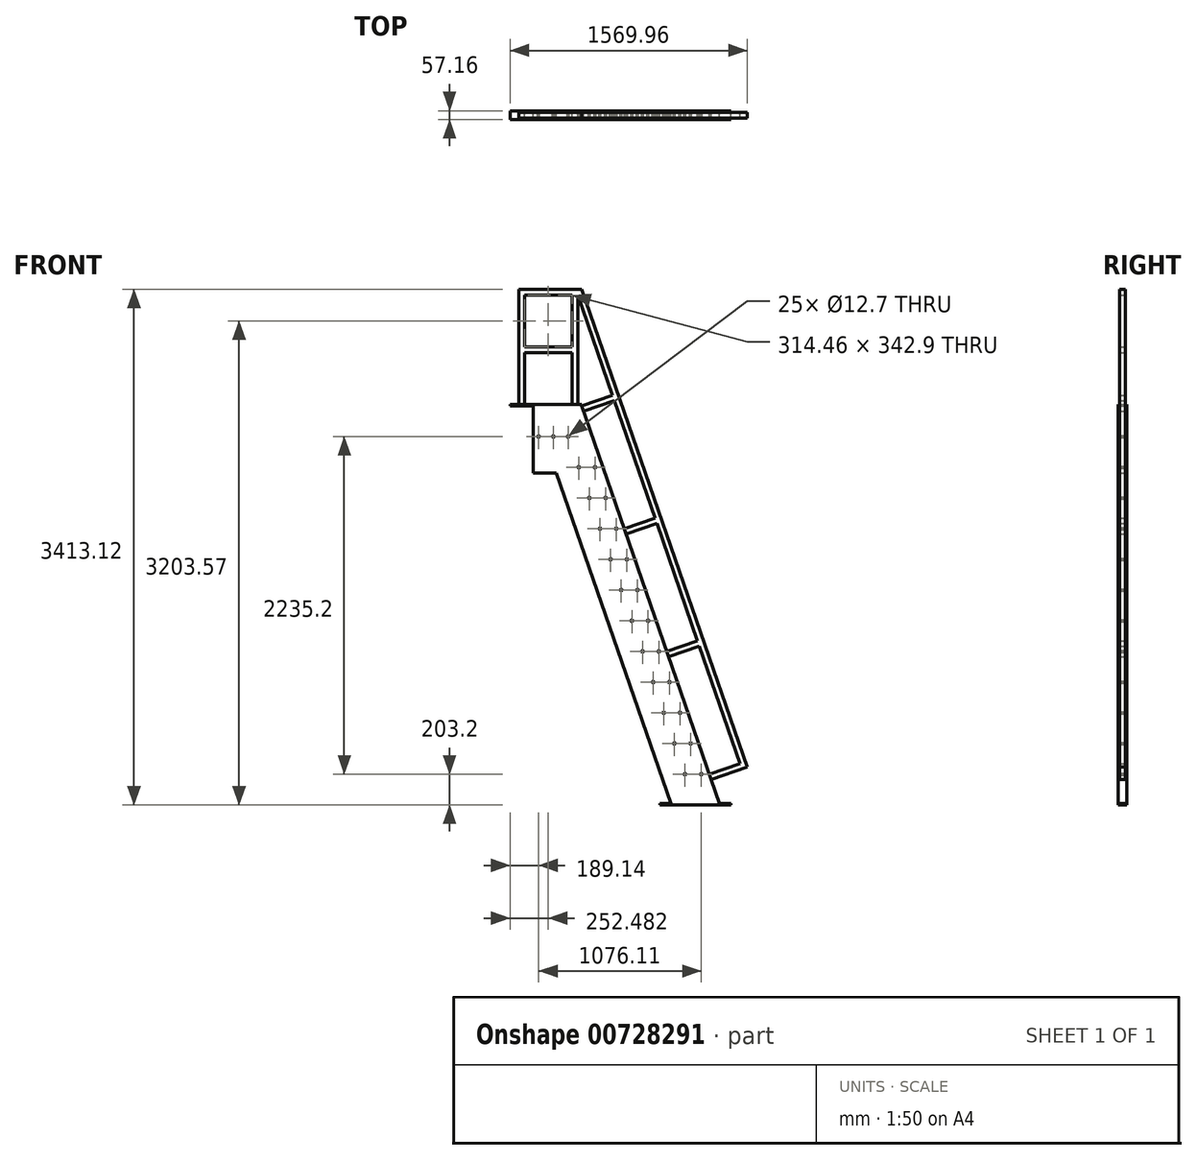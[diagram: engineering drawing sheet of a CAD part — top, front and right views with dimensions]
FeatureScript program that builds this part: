
annotation { "Feature Type Name" : "Feature", "Feature Type Description" : "" }
export const myFeature = defineFeature(function(context is Context, id is Id, definition is map)
    precondition{}
    {
        {
            var Q0;
            Q0=qCreatedBy(makeId("Front.planeOp"),FACE);
            var sketch = newSketch(context, id + "F0", { "sketchPlane" : qUnion([Q0])});
            skLineSegment(sketch, "E0", {"start": v(0, 2641.6) * mm, "end": v(0, 0) * mm, "construction": true});
            skLineSegment(sketch, "E1", {"start": v(0, 0) * mm, "end": v(914.4, 0) * mm, "construction": true});
            skLineSegment(sketch, "E2", {"start": v(0, 2641.6) * mm, "end": v(914.4, 0) * mm});
            skLineSegment(sketch, "E3", {"start": v(0, 2641.6) * mm, "end": v(322.54, 2641.6) * mm});
            skLineSegment(sketch, "E4", {"start": v(914.4, 0) * mm, "end": v(1236.94, 0) * mm});
            skLineSegment(sketch, "E5", {"start": v(322.54, 2641.6) * mm, "end": v(565.8, 1938.87) * mm});
            skLineSegment(sketch, "E6", {"start": v(0, 2641.6) * mm, "end": v(0, 2438.4) * mm, "construction": true});
            skLineSegment(sketch, "E7", {"start": v(0, 2438.4) * mm, "end": v(392.88, 2438.4) * mm, "construction": true});
            skLineSegment(sketch, "E8", {"start": v(0, 2438.4) * mm, "end": v(0, 2235.2) * mm, "construction": true});
            skLineSegment(sketch, "E9", {"start": v(0, 2235.2) * mm, "end": v(914.4, 2235.2) * mm, "construction": true});
            skLineSegment(sketch, "E10.0", {"start": v(0, 2032) * mm, "end": v(914.4, 2032) * mm, "construction": true});
            skLineSegment(sketch, "E11.0", {"start": v(0, 1828.8) * mm, "end": v(914.4, 1828.8) * mm, "construction": true});
            skLineSegment(sketch, "E12.0", {"start": v(0, 1625.6) * mm, "end": v(914.4, 1625.6) * mm, "construction": true});
            skLineSegment(sketch, "E13.0", {"start": v(0, 1422.4) * mm, "end": v(914.4, 1422.4) * mm, "construction": true});
            skLineSegment(sketch, "E14.0", {"start": v(0, 1219.2) * mm, "end": v(914.4, 1219.2) * mm, "construction": true});
            skLineSegment(sketch, "E15.0", {"start": v(0, 1016) * mm, "end": v(914.4, 1016) * mm, "construction": true});
            skLineSegment(sketch, "E16.0", {"start": v(0, 812.8) * mm, "end": v(955.6, 812.8) * mm, "construction": true});
            skLineSegment(sketch, "E17.0", {"start": v(0, 609.6) * mm, "end": v(1025.93, 609.6) * mm, "construction": true});
            skLineSegment(sketch, "E18", {"start": v(0, 609.6) * mm, "end": v(0, 406.4) * mm, "construction": true});
            skLineSegment(sketch, "E19", {"start": v(0, 406.4) * mm, "end": v(1272.26, 406.4) * mm, "construction": true});
            skLineSegment(sketch, "E20.0", {"start": v(0, 203.2) * mm, "end": v(1272.26, 203.2) * mm, "construction": true});
            skLineSegment(sketch, "E21", {"start": v(161.27, 2641.6) * mm, "end": v(1075.67, 0) * mm, "construction": true});
            skLineSegment(sketch, "E22.0", {"start": v(257.28, 2674.83) * mm, "end": v(1171.68, 33.23) * mm, "construction": true});
            skCircle(sketch, "E23", {"center": v(935, 406.4) * mm, "radius": 6.35 * mm});
            skCircle(sketch, "E24", {"center": v(1042.51, 406.4) * mm, "radius": 6.35 * mm});
            skCircle(sketch, "E25", {"center": v(1005.33, 203.2) * mm, "radius": 6.35 * mm});
            skCircle(sketch, "E26", {"center": v(1112.85, 203.2) * mm, "radius": 6.35 * mm});
            skLineSegment(sketch, "E27", {"start": v(322.54, 2641.6) * mm, "end": v(322.54, 2651.13) * mm});
            skLineSegment(sketch, "E28", {"start": v(322.54, 2651.13) * mm, "end": v(0, 2651.13) * mm});
            skLineSegment(sketch, "E29", {"start": v(0, 2651.13) * mm, "end": v(0, 2641.6) * mm});
            skLineSegment(sketch, "E30", {"start": v(0, 2651.13) * mm, "end": v(-152.4, 2651.13) * mm});
            skLineSegment(sketch, "E31", {"start": v(-152.4, 2651.13) * mm, "end": v(-152.4, 2641.6) * mm});
            skLineSegment(sketch, "E32", {"start": v(-152.4, 2641.6) * mm, "end": v(0, 2641.6) * mm});
            skLineSegment(sketch, "E33", {"start": v(914.4, 0) * mm, "end": v(838.2, 0) * mm});
            skLineSegment(sketch, "E34", {"start": v(838.2, 0) * mm, "end": v(838.2, 9.53) * mm});
            skLineSegment(sketch, "E35", {"start": v(838.2, 9.53) * mm, "end": v(911.1, 9.53) * mm});
            skLineSegment(sketch, "E36", {"start": v(1233.65, 9.53) * mm, "end": v(1309.85, 9.53) * mm});
            skLineSegment(sketch, "E37", {"start": v(1309.85, 9.53) * mm, "end": v(1309.85, 0) * mm});
            skLineSegment(sketch, "E38", {"start": v(1309.85, 0) * mm, "end": v(1236.94, 0) * mm});
            skLineSegment(sketch, "E39", {"start": v(-95.25, 2651.13) * mm, "end": v(-95.25, 3413.13) * mm});
            skLineSegment(sketch, "E40", {"start": v(-95.25, 3413.13) * mm, "end": v(322.54, 3413.13) * mm});
            skLineSegment(sketch, "E41.trimOffspring", {"start": v(955.6, 812.8) * mm, "end": v(1236.94, 0) * mm});
            skLineSegment(sketch, "E42.trimOffspring", {"start": v(603.9, 1828.8) * mm, "end": v(917.5, 922.87) * mm});
            skLineSegment(sketch, "E43", {"start": v(565.8, 1938.87) * mm, "end": v(603.9, 1828.8) * mm});
            skLineSegment(sketch, "E44", {"start": v(917.5, 922.87) * mm, "end": v(955.6, 812.8) * mm});
            skCircle(sketch, "E45", {"center": v(231.61, 2438.4) * mm, "radius": 6.35 * mm});
            skCircle(sketch, "E46", {"center": v(301.95, 2235.2) * mm, "radius": 6.35 * mm});
            skCircle(sketch, "E47", {"center": v(409.46, 2235.2) * mm, "radius": 6.35 * mm});
            skCircle(sketch, "E48", {"center": v(372.29, 2032) * mm, "radius": 6.35 * mm});
            skCircle(sketch, "E49", {"center": v(479.8, 2032) * mm, "radius": 6.35 * mm});
            skCircle(sketch, "E50", {"center": v(442.63, 1828.8) * mm, "radius": 6.35 * mm});
            skCircle(sketch, "E51", {"center": v(550.14, 1828.8) * mm, "radius": 6.35 * mm});
            skCircle(sketch, "E52", {"center": v(512.96, 1625.6) * mm, "radius": 6.35 * mm});
            skCircle(sketch, "E53", {"center": v(620.48, 1625.6) * mm, "radius": 6.35 * mm});
            skCircle(sketch, "E54", {"center": v(583.3, 1422.4) * mm, "radius": 6.35 * mm});
            skCircle(sketch, "E55", {"center": v(690.82, 1422.4) * mm, "radius": 6.35 * mm});
            skCircle(sketch, "E56", {"center": v(653.64, 1219.2) * mm, "radius": 6.35 * mm});
            skCircle(sketch, "E57", {"center": v(761.16, 1219.2) * mm, "radius": 6.35 * mm});
            skCircle(sketch, "E58", {"center": v(723.98, 1016) * mm, "radius": 6.35 * mm});
            skCircle(sketch, "E59", {"center": v(831.5, 1016) * mm, "radius": 6.35 * mm});
            skCircle(sketch, "E60", {"center": v(794.32, 812.8) * mm, "radius": 6.35 * mm});
            skCircle(sketch, "E61", {"center": v(901.83, 812.8) * mm, "radius": 6.35 * mm});
            skCircle(sketch, "E62", {"center": v(864.66, 609.6) * mm, "radius": 6.35 * mm});
            skCircle(sketch, "E63", {"center": v(972.17, 609.6) * mm, "radius": 6.35 * mm});
            skLineSegment(sketch, "E64", {"start": v(322.54, 3413.13) * mm, "end": v(1405.1, 285.75) * mm});
            skLineSegment(sketch, "E65", {"start": v(1166.6, 203.2) * mm, "end": v(1405.1, 285.75) * mm});
            skLineSegment(sketch, "E66", {"start": v(885.25, 1016) * mm, "end": v(1123.74, 1098.55) * mm});
            skLineSegment(sketch, "E67", {"start": v(603.9, 1828.8) * mm, "end": v(842.39, 1911.35) * mm});
            skLineSegment(sketch, "E68", {"start": v(322.54, 2641.6) * mm, "end": v(561.03, 2724.15) * mm});
            skLineSegment(sketch, "E69.0", {"start": v(335, 2605.6) * mm, "end": v(573.5, 2688.15) * mm});
            skLineSegment(sketch, "E70.0", {"start": v(616.36, 1792.8) * mm, "end": v(854.85, 1875.35) * mm});
            skLineSegment(sketch, "E71.0", {"start": v(897.72, 980) * mm, "end": v(1136.2, 1062.55) * mm});
            skLineSegment(sketch, "E72.0", {"start": v(1179.07, 167.2) * mm, "end": v(1417.56, 249.75) * mm});
            skLineSegment(sketch, "E73.0", {"start": v(295.41, 3375.03) * mm, "end": v(1369.1, 273.3) * mm});
            skLineSegment(sketch, "E73.1", {"start": v(-57.15, 3375.03) * mm, "end": v(295.41, 3375.03) * mm});
            skLineSegment(sketch, "E73.2", {"start": v(-57.15, 2651.13) * mm, "end": v(-57.15, 3375.03) * mm});
            skLineSegment(sketch, "E74", {"start": v(1405.1, 285.75) * mm, "end": v(1417.56, 249.75) * mm});
            skLineSegment(sketch, "E75", {"start": v(295.41, 3375.03) * mm, "end": v(295.41, 2651.13) * mm});
            skLineSegment(sketch, "E76.0", {"start": v(257.31, 3375.03) * mm, "end": v(257.31, 2651.13) * mm});
            skLineSegment(sketch, "E77", {"start": v(-57.15, 3375.03) * mm, "end": v(-57.15, 3032.13) * mm});
            skLineSegment(sketch, "E78", {"start": v(-57.15, 3032.13) * mm, "end": v(257.31, 3032.13) * mm});
            skLineSegment(sketch, "E79.0", {"start": v(-57.15, 2994.03) * mm, "end": v(257.31, 2994.03) * mm});
            skLineSegment(sketch, "E80", {"start": v(0, 2641.6) * mm, "end": v(0, 2197.1) * mm});
            skLineSegment(sketch, "E81", {"start": v(0, 2197.1) * mm, "end": v(153.87, 2197.1) * mm});
            skLineSegment(sketch, "E82.0", {"start": v(74.26, 2611.48) * mm, "end": v(988.66, -30.12) * mm, "construction": true});
            skLineSegment(sketch, "E83.0", {"start": v(-12.75, 2581.36) * mm, "end": v(901.65, -60.24) * mm, "construction": true});
            skCircle(sketch, "E84", {"center": v(36.74, 2438.4) * mm, "radius": 6.35 * mm});
            skCircle(sketch, "E85", {"center": v(134.18, 2438.4) * mm, "radius": 6.35 * mm});
            skLineSegment(sketch, "E86.left", {"start": v(0, 2419.35) * mm, "end": v(0, 2457.45) * mm});
            skSolve(sketch);
        }
        {
            var Q0;
            {var subQ0=sQuery(id+"F0.wireOp",EDGE,"E33");Q0=makeQuery(id+"F0.imprint","IMPRINT",FACE,{"disambiguationData":[TD([[makeQuery(id+"F0.imprint","IMPRINT",EDGE,{"derivedFrom":subQ0}),-1.0]])]});}
            var Q1;
            {var subQ0=sQuery(id+"F0.wireOp",EDGE,"E36");Q1=makeQuery(id+"F0.imprint","IMPRINT",FACE,{"disambiguationData":[TD([[makeQuery(id+"F0.imprint","IMPRINT",EDGE,{"derivedFrom":subQ0}),-1.0]])]});}
            var Q2;
            {var subQ0=sQuery(id+"F0.wireOp",EDGE,"E80");Q2=makeQuery(id+"F0.imprint","IMPRINT",FACE,{"disambiguationData":[TD([[makeQuery(id+"F0.imprint","IMPRINT",EDGE,{"derivedFrom":subQ0}),1.0]])]});}
            var Q3;
            {var subQ4=sQuery(id+"F0.wireOp",EDGE,"E29");Q3=makeQuery(id+"F0.imprint","IMPRINT",FACE,{"disambiguationData":[TD([[makeQuery(id+"F0.imprint","IMPRINT",EDGE,{"derivedFrom":subQ4}),-1.0]])]});}
            var Q4;
            Q4=makeQuery(id+"F0.imprint","IMPRINT",FACE,{"disambiguationData":[TD([[makeQuery(id+"F0.imprint","IMPRINT",EDGE,{"derivedFrom":sQuery(id+"F0.wireOp",EDGE,"E3")}),1.0]])]});
            var Q5;
            {var subQ6=sQuery(id+"F0.wireOp",EDGE,"E3");Q5=makeQuery(id+"F0.imprint","IMPRINT",FACE,{"disambiguationData":[TD([[makeQuery(id+"F0.imprint","IMPRINT",EDGE,{"derivedFrom":subQ6}),-1.0]])]});}
            extrude(context, id + "F1", {"entities" : qUnion([Q0, Q1, Q2, Q3, Q4, Q5]), "endBound" : BoundingType.SYMMETRIC, "depth" : 57.15 * mm, "offsetDistance" : 25.4 * mm});
        }
        {
            var Q0;
            {var subQ0=sQuery(id+"F0.wireOp",EDGE,"E67");var subQ1=sQuery(id+"F0.wireOp",EDGE,"E64");var subQ2=makeQuery(id+"F0.imprint","INTERSECT",VERTEX,{"derivedFrom":[subQ1,subQ0]});Q0=makeQuery(id+"F0.imprint","IMPRINT",FACE,{"disambiguationData":[TD([[makeQuery(id+"F0.imprint","IMPRINT",EDGE,{"disambiguationData":[TD([[subQ2,1.0]])],"derivedFrom":subQ1}),-1.0]])]});}
            var Q1;
            {var subQ0=sQuery(id+"F0.wireOp",EDGE,"E66");var subQ1=sQuery(id+"F0.wireOp",EDGE,"E64");var subQ2=makeQuery(id+"F0.imprint","INTERSECT",VERTEX,{"derivedFrom":[subQ1,subQ0]});Q1=makeQuery(id+"F0.imprint","IMPRINT",FACE,{"disambiguationData":[TD([[makeQuery(id+"F0.imprint","IMPRINT",EDGE,{"disambiguationData":[TD([[subQ2,1.0]])],"derivedFrom":subQ1}),-1.0]])]});}
            var Q2;
            {var subQ0=sQuery(id+"F0.wireOp",EDGE,"E67");var subQ1=sQuery(id+"F0.wireOp",EDGE,"E64");var subQ2=makeQuery(id+"F0.imprint","INTERSECT",VERTEX,{"derivedFrom":[subQ1,subQ0]});Q2=makeQuery(id+"F0.imprint","IMPRINT",FACE,{"disambiguationData":[TD([[makeQuery(id+"F0.imprint","IMPRINT",EDGE,{"disambiguationData":[TD([[subQ2,-1.0]])],"derivedFrom":subQ1}),-1.0]])]});}
            var Q3;
            {var subQ1=sQuery(id+"F0.wireOp",EDGE,"E42.trimOffspring");var subQ3=sQuery(id+"F0.wireOp",EDGE,"E70.0");var subQ4=makeQuery(id+"F0.imprint","INTERSECT",VERTEX,{"derivedFrom":[subQ1,subQ3]});Q3=makeQuery(id+"F0.imprint","IMPRINT",FACE,{"disambiguationData":[TD([[makeQuery(id+"F0.imprint","IMPRINT",EDGE,{"disambiguationData":[TD([[subQ4,-1.0]])],"derivedFrom":subQ3}),1.0]])]});}
            var Q4;
            {var subQ1=sQuery(id+"F0.wireOp",EDGE,"E5");var subQ3=sQuery(id+"F0.wireOp",EDGE,"E69.0");var subQ4=makeQuery(id+"F0.imprint","INTERSECT",VERTEX,{"derivedFrom":[subQ1,subQ3]});Q4=makeQuery(id+"F0.imprint","IMPRINT",FACE,{"disambiguationData":[TD([[makeQuery(id+"F0.imprint","IMPRINT",EDGE,{"disambiguationData":[TD([[subQ4,-1.0]])],"derivedFrom":subQ3}),1.0]])]});}
            var Q5;
            {var subQ4=sQuery(id+"F0.wireOp",EDGE,"E75");Q5=makeQuery(id+"F0.imprint","IMPRINT",FACE,{"disambiguationData":[TD([[makeQuery(id+"F0.imprint","IMPRINT",EDGE,{"derivedFrom":subQ4}),-1.0]])]});}
            var Q6;
            {var subQ0=sQuery(id+"F0.wireOp",EDGE,"E78");Q6=makeQuery(id+"F0.imprint","IMPRINT",FACE,{"disambiguationData":[TD([[makeQuery(id+"F0.imprint","IMPRINT",EDGE,{"derivedFrom":subQ0}),-1.0]])]});}
            var Q7;
            {var subQ0=sQuery(id+"F0.wireOp",EDGE,"E68");var subQ1=sQuery(id+"F0.wireOp",EDGE,"E64");var subQ2=makeQuery(id+"F0.imprint","INTERSECT",VERTEX,{"derivedFrom":[subQ1,subQ0]});Q7=makeQuery(id+"F0.imprint","IMPRINT",FACE,{"disambiguationData":[TD([[makeQuery(id+"F0.imprint","IMPRINT",EDGE,{"disambiguationData":[TD([[subQ2,-1.0]])],"derivedFrom":subQ1}),-1.0]])]});}
            var Q8;
            {var subQ13=sQuery(id+"F0.wireOp",EDGE,"E39");Q8=makeQuery(id+"F0.imprint","IMPRINT",FACE,{"disambiguationData":[TD([[makeQuery(id+"F0.imprint","IMPRINT",EDGE,{"derivedFrom":subQ13}),-1.0]])]});}
            var Q9;
            {var subQ1=sQuery(id+"F0.wireOp",EDGE,"E64");var subQ3=sQuery(id+"F0.wireOp",EDGE,"E71.0");var subQ4=makeQuery(id+"F0.imprint","INTERSECT",VERTEX,{"derivedFrom":[subQ1,subQ3]});Q9=makeQuery(id+"F0.imprint","IMPRINT",FACE,{"disambiguationData":[TD([[makeQuery(id+"F0.imprint","IMPRINT",EDGE,{"disambiguationData":[TD([[subQ4,1.0]])],"derivedFrom":subQ3}),-1.0]])]});}
            var Q10;
            {var subQ0=sQuery(id+"F0.wireOp",EDGE,"E66");var subQ1=sQuery(id+"F0.wireOp",EDGE,"E64");var subQ2=makeQuery(id+"F0.imprint","INTERSECT",VERTEX,{"derivedFrom":[subQ1,subQ0]});Q10=makeQuery(id+"F0.imprint","IMPRINT",FACE,{"disambiguationData":[TD([[makeQuery(id+"F0.imprint","IMPRINT",EDGE,{"disambiguationData":[TD([[subQ2,-1.0]])],"derivedFrom":subQ1}),-1.0]])]});}
            var Q11;
            {var subQ0=sQuery(id+"F0.wireOp",EDGE,"E66");var subQ1=sQuery(id+"F0.wireOp",EDGE,"E42.trimOffspring");var subQ2=makeQuery(id+"F0.imprint","INTERSECT",VERTEX,{"derivedFrom":[subQ1,subQ0]});Q11=makeQuery(id+"F0.imprint","IMPRINT",FACE,{"disambiguationData":[TD([[makeQuery(id+"F0.imprint","IMPRINT",EDGE,{"disambiguationData":[TD([[subQ2,-1.0]])],"derivedFrom":subQ1}),1.0]])]});}
            var Q12;
            {var subQ5=sQuery(id+"F0.wireOp",EDGE,"E72.0");Q12=makeQuery(id+"F0.imprint","IMPRINT",FACE,{"disambiguationData":[TD([[makeQuery(id+"F0.imprint","IMPRINT",EDGE,{"derivedFrom":subQ5}),1.0]])]});}
            extrude(context, id + "F2", {"entities" : qUnion([Q0, Q1, Q2, Q3, Q4, Q5, Q6, Q7, Q8, Q9, Q10, Q11, Q12]), "operationType" : NewBodyOperationType.ADD, "endBound" : BoundingType.SYMMETRIC, "depth" : 38.1 * mm, "offsetDistance" : 25.4 * mm});
        }
    });
